FCSTD DOCUMENT  (FreeCAD 0.16R6704 (Git))
Label: insharp
License: All rights reserved
LicenseURL: http://en.wikipedia.org/wiki/All_rights_reserved
objects: Sketcher::SketchObject×1
note: 1 computed .brp shape members not serialized (recipe doc carries the construction recipe); baked Part::Feature solids carry a one-line shape summary decoded from their .brp

FEATURE [Sketcher::SketchObject] Sketch
  sketch-geometry (8):
    g0: LineSegment StartX=10 StartY=0 StartZ=0 EndX=8 EndY=-3.4641 EndZ=0
    g1: LineSegment StartX=8 StartY=-3.4641 StartZ=0 EndX=2 EndY=-3.4641 EndZ=0
    g2: LineSegment StartX=2 StartY=-3.4641 StartZ=0 EndX=0 EndY=0 EndZ=0
    g3: LineSegment StartX=0 StartY=0 StartZ=0 EndX=3 EndY=0 EndZ=0
    g4: LineSegment StartX=3 StartY=0 StartZ=0 EndX=2.2 EndY=-1.83303 EndZ=0
    g5: LineSegment StartX=2.2 StartY=-1.83303 StartZ=0 EndX=7.8 EndY=-1.83303 EndZ=0
    g6: LineSegment StartX=7.8 StartY=-1.83303 StartZ=0 EndX=7 EndY=0 EndZ=0
    g7: LineSegment StartX=7 StartY=0 StartZ=0 EndX=10 EndY=0 EndZ=0
  constraints (23):
    c: PointOnObject(g0,g-1)
    c: Coincident(g0,g1)
    c: Horizontal(g1)
    c: Coincident(g1,g2)
    c: Angle(g2,g-1) = 1.0472
    c: DistanceX(g-1,g0) = 10
    c: Distance(g0) = 4
    c: Coincident(g2,g-1)
    c: Equal(g2,g0)
    c: Coincident(g-1,g3)
    c: PointOnObject(g3,g-1)
    c: Coincident(g3,g4)
    c: Coincident(g4,g5)
    c: Horizontal(g5)
    c: Coincident(g5,g6)
    c: PointOnObject(g6,g-1)
    c: Coincident(g6,g7)
    c: Coincident(g7,g0)
    c: Equal(g3,g7)
    c: DistanceX(g3,g3) = 3
    c: Equal(g4,g6)
    c: Distance(g4) = 2
    c: DistanceX(g5,g5) = 5.6
